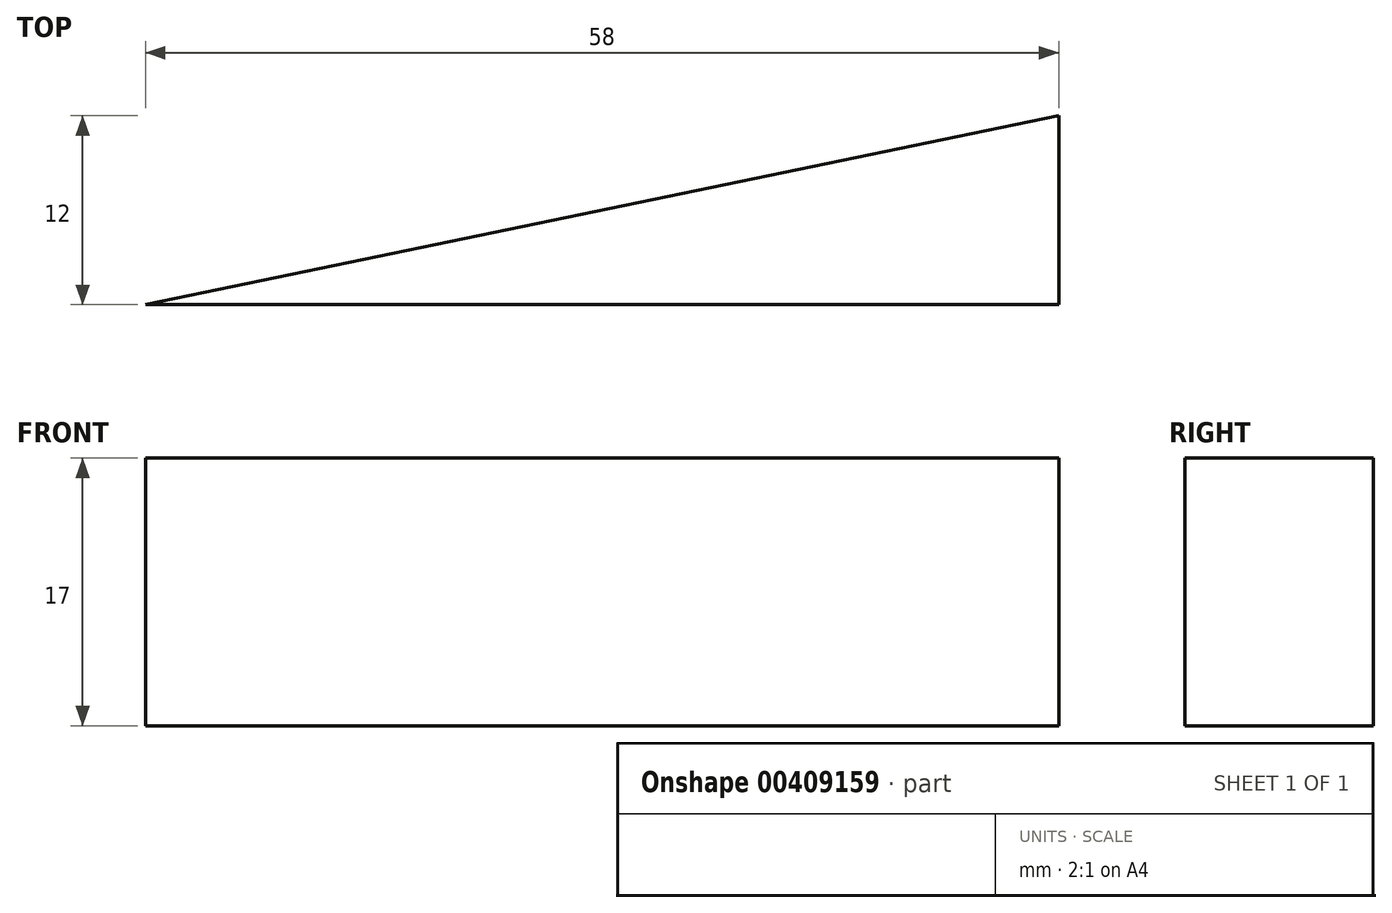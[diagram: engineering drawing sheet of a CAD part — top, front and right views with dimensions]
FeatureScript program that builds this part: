
annotation { "Feature Type Name" : "Feature", "Feature Type Description" : "" }
export const myFeature = defineFeature(function(context is Context, id is Id, definition is map)
    precondition{}
    {
        {
            var Q0;
            Q0=qCreatedBy(makeId("Top.planeOp"),FACE);
            var sketch = newSketch(context, id + "F0", { "sketchPlane" : qUnion([Q0])});
            skLineSegment(sketch, "E0", {"start": v(29, 6) * mm, "end": v(-29, -6) * mm});
            skLineSegment(sketch, "E1", {"start": v(-29, -6) * mm, "end": v(29, -6) * mm});
            skLineSegment(sketch, "E2", {"start": v(29, -6) * mm, "end": v(29, 6) * mm});
            skSolve(sketch);
        }
        {
            var Q0;
            Q0=makeQuery(id+"F0.imprint","IMPRINT",FACE,{"disambiguationData":[TD([[makeQuery(id+"F0.imprint","IMPRINT",EDGE,{"derivedFrom":sQuery(id+"F0.wireOp",EDGE,"E0")}),1.0]])]});
            extrude(context, id + "F1", {"entities" : qUnion([Q0]), "depth" : 17 * mm, "offsetDistance" : 25 * mm, "symmetric" : true});
        }
    });
